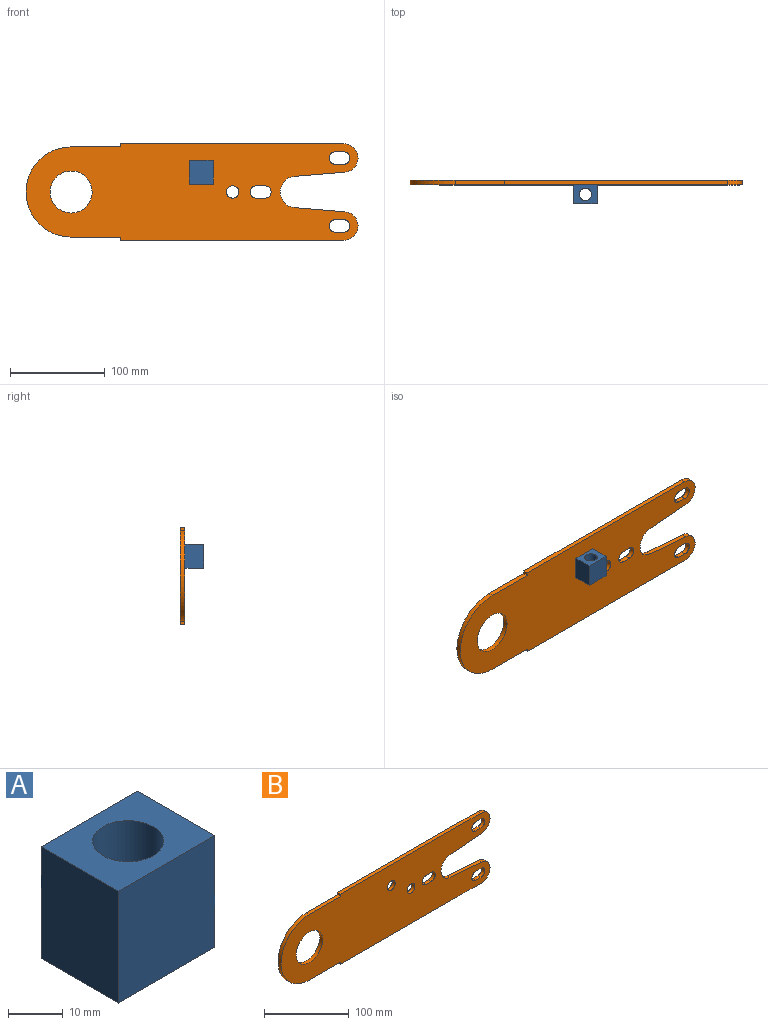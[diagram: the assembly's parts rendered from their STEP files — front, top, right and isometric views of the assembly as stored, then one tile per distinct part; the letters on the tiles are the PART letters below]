
ASSEMBLY  parts=2 mates=1
PART A: 7 faces, bbox 25x20x25 mm
  f0: plane 25x20mm, normal (1,0,0), area 500mm2, adj f1,f3,f4,f5
  f1: plane 25x20mm, normal (0,0,1), area 367.3mm2, adj f0,f2,f4,f5,f6
  f2: plane 25x20mm, normal (-1,0,0), area 500mm2, adj f1,f3,f4,f5
  f3: plane 25x20mm, normal (0,0,-1), area 367.3mm2, adj f0,f2,f4,f5,f6
  f4: plane 25x25mm, normal (0,-1,0), area 625mm2, adj f0,f1,f2,f3
  f5: plane 25x25mm, normal (0,1,0), area 625mm2, adj f0,f1,f2,f3
  f6: cylinder r=6.5mm len=25mm, axis (0,0,1), area 1021mm2, adj f1,f3
PART B: 29 faces, bbox 349.6x5x101.5 mm
  f0: cylinder r=6.5mm len=13mm, axis (0,1,0), area 102.1mm2, adj f1,f26,f27,f28
  f1: plane 9x5mm, normal (0,0,-1), area 45mm2, adj f0,f2,f27,f28
  f2: cylinder r=6.5mm len=13mm, axis (0,1,0), area 102.1mm2, adj f1,f26,f27,f28
  f3: cylinder r=6.5mm len=13mm, axis (0,1,0), area 102.1mm2, adj f4,f20,f27,f28
  f4: plane 9x5mm, normal (0,0,-1), area 45mm2, adj f3,f5,f27,f28
  f5: cylinder r=6.5mm len=13mm, axis (0,1,0), area 102.1mm2, adj f4,f20,f27,f28
  f6: plane 52.13x5mm, normal (0,0,1), area 260.6mm2, adj f7,f24,f27,f28
  f7: cylinder r=47.5mm len=95mm, axis (0,1,0), area 746.1mm2, adj f6,f8,f27,f28
  f8: plane 52.13x5mm, normal (0,0,-1), area 260.6mm2, adj f7,f9,f27,f28
  f9: plane 5x3.25mm, normal (-1,0,0), area 16.3mm2, adj f8,f10,f27,f28
  f10: plane 235x5mm, normal (0,0,-1), area 1175mm2, adj f9,f11,f27,f28
  f11: cylinder r=15mm len=29.95mm, axis (0,1,0), area 229.5mm2, adj f10,f12,f27,f28
  f12: plane 53.08x5mm, normal (0.08,0,1), area 266.3mm2, adj f11,f13,f27,f28
  f13: cylinder r=16.5mm len=32.89mm, axis (0,1,0), area 245.7mm2, adj f12,f14,f27,f28
  f14: plane 53.08x5mm, normal (0.08,0,-1), area 266.3mm2, adj f13,f15,f27,f28
  f15: cylinder r=15mm len=29.95mm, axis (0,1,0), area 229.5mm2, adj f14,f16,f27,f28
  f16: plane 235x5mm, normal (0,0,1), area 1175mm2, adj f15,f24,f27,f28
  f17: plane 9x5mm, normal (0,0,1), area 45mm2, adj f18,f25,f27,f28
  f18: cylinder r=6.5mm len=13mm, axis (0,1,0), area 102.1mm2, adj f17,f19,f27,f28
  f19: plane 9x5mm, normal (0,0,-1), area 45mm2, adj f18,f25,f27,f28
  f20: plane 9x5mm, normal (0,0,1), area 45mm2, adj f3,f5,f27,f28
  f21: cylinder r=6.5mm len=13mm, axis (0,1,0), area 204.2mm2, adj f27,f28
  f22: cylinder r=6.5mm len=13mm, axis (0,1,0), area 204.2mm2, adj f27,f28
  f23: cylinder r=22.12mm len=44.25mm, axis (0,1,0), area 695.1mm2, adj f27,f28
  f24: plane 5x3.25mm, normal (-1,0,0), area 16.3mm2, adj f6,f16,f27,f28
  f25: cylinder r=6.5mm len=13mm, axis (0,1,0), area 102.1mm2, adj f17,f19,f27,f28
  f26: plane 9x5mm, normal (0,0,1), area 45mm2, adj f0,f2,f27,f28
  f27: plane 349.63x101.5mm, normal (0,-1,0), area 28193.8mm2, adj f0,f1,f2,f3,f4,f5,f6,f7
  f28: plane 349.63x101.5mm, normal (0,1,0), area 28193.8mm2, adj f0,f1,f2,f3,f4,f5,f6,f7
PLACE A t=(86.02,35.92,12.38)mm
PLACE B t=(-51.1,40.92,-8.37)mm
MATE fastened A.f5 <-> B.f22  axis (0,1,0) through (86.02,35.92,12.38)mm
